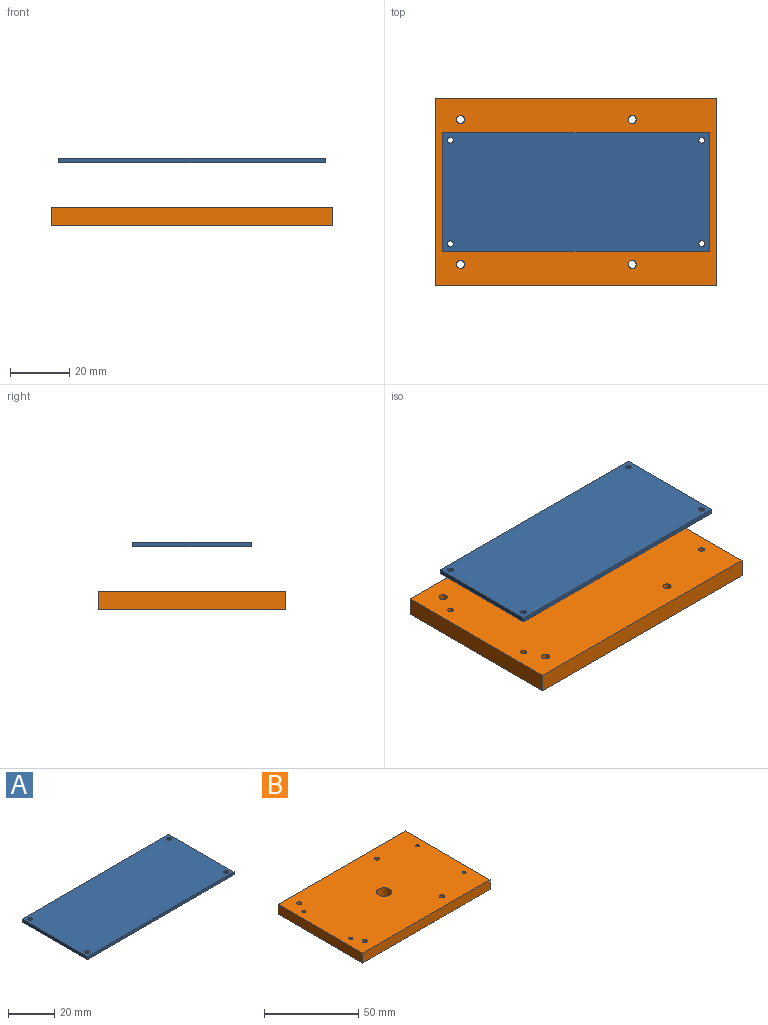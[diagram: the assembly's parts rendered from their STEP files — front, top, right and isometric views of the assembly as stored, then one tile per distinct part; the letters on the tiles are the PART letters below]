
ASSEMBLY  parts=2 mates=1
PART A: 10 faces, bbox 90x40x1.6 mm
  f0: plane 90x1.6mm, normal (0,-1,0), area 144mm2, adj f1,f3,f4,f5
  f1: plane 40x1.6mm, normal (1,0,0), area 64mm2, adj f0,f2,f4,f5
  f2: plane 90x1.6mm, normal (0,1,0), area 144mm2, adj f1,f3,f4,f5
  f3: plane 40x1.6mm, normal (-1,0,0), area 64mm2, adj f0,f2,f4,f5
  f4: plane 90x40mm, normal (0,0,-1), area 3587.4mm2, adj f0,f1,f2,f3,f6,f7,f8,f9
  f5: plane 90x40mm, normal (0,0,1), area 3587.4mm2, adj f0,f1,f2,f3,f6,f7,f8,f9
  f6: cylinder r=1mm len=2mm, axis (0,0,1), area 10.1mm2, adj f4,f5
  f7: cylinder r=1mm len=2mm, axis (0,0,1), area 10.1mm2, adj f4,f5
  f8: cylinder r=1mm len=2mm, axis (0,0,1), area 10.1mm2, adj f4,f5
  f9: cylinder r=1mm len=2mm, axis (0,0,1), area 10.1mm2, adj f4,f5
PART B: 15 faces, bbox 95.3x63.5x6.4 mm
  f0: plane 95.25x6.35mm, normal (0,1,0), area 604.8mm2, adj f1,f3,f4,f5
  f1: plane 63.5x6.35mm, normal (-1,0,0), area 403.2mm2, adj f0,f2,f4,f5
  f2: plane 95.25x6.35mm, normal (0,-1,0), area 604.8mm2, adj f1,f3,f4,f5
  f3: plane 63.5x6.35mm, normal (1,0,0), area 403.2mm2, adj f0,f2,f4,f5
  f4: plane 95.25x63.5mm, normal (0,0,-1), area 5962.6mm2, adj f0,f1,f2,f3,f6,f7,f8,f9
  f5: plane 95.25x63.5mm, normal (0,0,1), area 5962.6mm2, adj f0,f1,f2,f3,f6,f7,f8,f9
  f6: cylinder r=1.38mm len=6.35mm, axis (0,0,1), area 54.9mm2, adj f4,f5
  f7: cylinder r=1.38mm len=6.35mm, axis (0,0,1), area 54.9mm2, adj f4,f5
  f8: cylinder r=1.38mm len=6.35mm, axis (0,0,1), area 54.9mm2, adj f4,f5
  f9: cylinder r=1.38mm len=6.35mm, axis (0,0,1), area 54.9mm2, adj f4,f5
  f10: cylinder r=1mm len=6.35mm, axis (0,0,1), area 39.9mm2, adj f4,f5
  f11: cylinder r=1mm len=6.35mm, axis (0,0,1), area 39.9mm2, adj f4,f5
  f12: cylinder r=1mm len=6.35mm, axis (0,0,1), area 39.9mm2, adj f4,f5
  f13: cylinder r=1mm len=6.35mm, axis (0,0,1), area 39.9mm2, adj f4,f5
  f14: cylinder r=3.97mm len=7.94mm, axis (0,0,1), area 158.3mm2, adj f4,f5
PLACE A t=(0,0,16.6)mm
PLACE B at identity fixed
MATE fastened A.f6 <-> B.f10  axis (0,0,1) through (-42.5,17.5,15)mm
